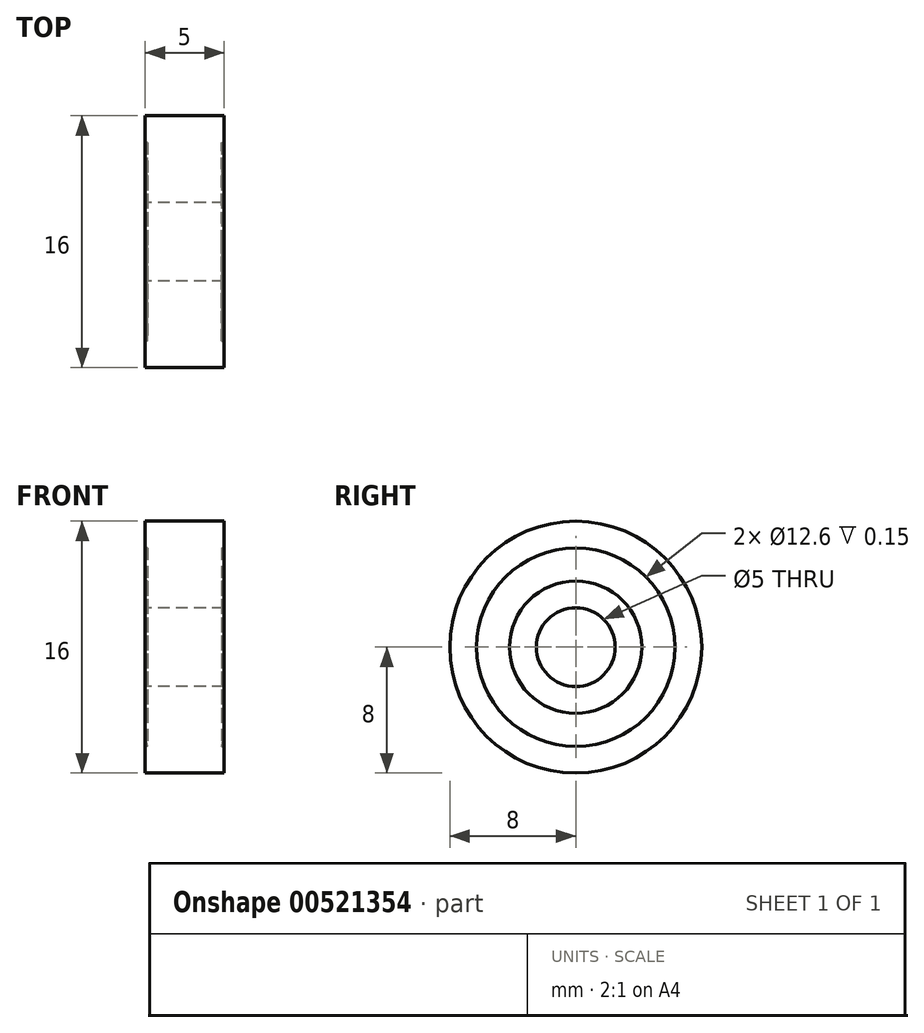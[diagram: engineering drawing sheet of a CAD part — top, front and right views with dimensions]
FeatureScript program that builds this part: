
annotation { "Feature Type Name" : "Feature", "Feature Type Description" : "" }
export const myFeature = defineFeature(function(context is Context, id is Id, definition is map)
    precondition{}
    {
        {
            var Q0;
            Q0=qCreatedBy(makeId("Front.planeOp"),FACE);
            var sketch = newSketch(context, id + "F0", { "sketchPlane" : qUnion([Q0])});
            skLineSegment(sketch, "E0", {"start": v(-17.4, 0) * mm, "end": v(25.76, 0) * mm, "construction": true});
            skLineSegment(sketch, "E1", {"start": v(0, 2.5) * mm, "end": v(-2.5, 2.5) * mm});
            skLineSegment(sketch, "E2", {"start": v(-2.5, 2.5) * mm, "end": v(-2.5, 4.2) * mm});
            skLineSegment(sketch, "E3", {"start": v(-2.5, 4.2) * mm, "end": v(-2.35, 4.2) * mm});
            skLineSegment(sketch, "E4", {"start": v(-2.35, 6.3) * mm, "end": v(-2.5, 6.3) * mm});
            skLineSegment(sketch, "E5", {"start": v(-2.5, 6.3) * mm, "end": v(-2.5, 8) * mm});
            skLineSegment(sketch, "E6", {"start": v(-2.5, 8) * mm, "end": v(0, 8) * mm});
            skLineSegment(sketch, "E7", {"start": v(0, 8) * mm, "end": v(0, 2.5) * mm});
            skArc(sketch, "E8", {"start": v(-2.35, 6.3) * mm, "mid": v(-2.5, 5.25) * mm, "end": v(-2.35, 4.2) * mm});
            skLineSegment(sketch, "E9", {"start": v(0, -15.75) * mm, "end": v(0, 21.22) * mm, "construction": true});
            skPoint(sketch, "E10", {"position": v(0, 5.25) * mm});
            skSolve(sketch);
        }
        {
            var Q0;
            Q0 = qSketchRegion(id + "F0", true);
            var Q1;
            Q1=sQuery(id+"F0.wireOp",EDGE,"E0");
            revolve(context, id + "F1", {"entities" : qUnion([Q0]), "axis" : qUnion([Q1]), "revolveType" : RevolveType.FULL});
        }
        {
            var Q0;
            Q0=makeQuery(id+"F1.opRevolve","SWEPT_BODY",BODY,{"disambiguationData":[OSD([sQuery(id+"F0.wireOp",EDGE,"E1"),sQuery(id+"F0.wireOp",EDGE,"E2"),sQuery(id+"F0.wireOp",EDGE,"E3"),sQuery(id+"F0.wireOp",EDGE,"E4"),sQuery(id+"F0.wireOp",EDGE,"E5"),sQuery(id+"F0.wireOp",EDGE,"E6"),sQuery(id+"F0.wireOp",EDGE,"E7"),sQuery(id+"F0.wireOp",EDGE,"E8")])]});
            var Q1;
            Q1=qCreatedBy(makeId("Right.planeOp"),FACE);
            mirror(context, id + "F2", {"operationType" : NewBodyOperationType.ADD, "entities" : qUnion([Q0]), "mirrorPlane" : qUnion([Q1])});
        }
    });
